# Revit family: Projector-DLP-Panasonic-1_Chip-Full_Brightness-Longer_Lasting_Laser_Performance-PT-FRZ60_SeriesX
name_source: partatom
category: Communication Devices
units: mm (PartAtom-declared; Revit-internal decimal feet)

## family parameters
Cut with Voids When Loaded = Yes
Host = Face
Maintain Annotation Orientation = No
OmniClass Number = 23.85.10.17.11.21
OmniClass Title = Data/Multi/Media Projectors
Part Type = Normal
Room Calculation Point = No
Round Connector Dimension = Use Diameter
Shared = No

## types (2) — shared parameters
352_mm = High_Ceiling_Height : 352_mm
392_mm = High_Ceiling_Height : 392_mm
432_mm = High_Ceiling_Height : 432_mm
A_Supplied_Max = 2.5118
A_Supplied_Min = 1.2598
Body Depth = 460 mm  [stored 1.50919 ft]
Ceiling Distance = 100 mm  [stored 0.328084 ft]
Chip Diagonal = 17 mm
Chip Quantity = 1
Clearance Value = 500 mm  [stored 1.64042 ft]
Const Length Projector Pan Handle = 2000 mm  [stored 6.56168 ft]
Const Length Projector Panning Base = 1000 mm  [stored 3.28084 ft]
Contrast Ratio = 20000
Date Last Modified = 2020/10/14
Depth = 492 mm
Equipment Abbreviation = LVP
Family Version = 1.0.0
HDMI In = HDMI 19-pin x 2 Compatible with HDCP 2.3, Deep Color, 4K/60p signal input*6, CEC supported
Height = 168 mm  [stored 0.551181 ft]
LAN = RJ‑45 x 1 for network connection, PJLink (class 2) compatible, 10Base‑T/100Base‑TX, Art-Net compatible
Lamp Life Economy = 24000
Lamp Life Full = 20000
Lamp Type = Laser diodes
Lens Type = Integrated
Manufacturer = Panasonic
Market = Commercial
Max Air Exhaust Volume = 285.00 CFM
Model Disclaimer = Contact Panasonic for more information
Motorized Zoom = No
Must be Level = No
Panasonic Logo Material = Paint - Panasonic Logo
Power Standby Eco = 1 W
Power Standby Normal = 10 W
Product Documentation Link = https://bizpartner.panasonic.net
Product Material = Plastic - Panasonic White
Product Page URL = https://panasonic.net
Provide Feedback = https://www.surveymonkey.com
Resolution Horizontal = 1920
Resolution Vertical = 1200
Technology = DLP™ chip x 1, DLP™ projection system
Temperature Max = 113 °F
Temperature Min = 32 °F
URL = http://panasonic.net
Width = 498 mm  [stored 1.63386 ft]
zero-valued in all types: Default Elevation

## per-type parameters (varying)
| type | Brightness Economy | Brightness Full | Description | Heat Load Active | Lamp Quantity | Noise in High Mode | Noise in Low Mode | P Type | Part Description | Power Active | Total Rated Watts | Weight |
| PT-FRZ60 | 4800 lm | 6000 lm | 6,000 Lumens, 16:10 Aspect Ratio, WUXGA, Projector, PT-FRZ60 | 1843.00 Btu/h | 4 | 35 | 30 | 60 | 6,000 Lumens, 16:10 Aspect Ratio, WUXGA, Projector, PT-FRZ60 | 540 W | 540 W | 35.50 lb |
| PT-FRZ50 | 4100 lm | 5200 lm | 5,200 Lumens, 16:10 Aspect Ratio, WUXGA, Projector, PT-FRZ50 | 1587.00 Btu/h | 2 | 32 | 27 | 50 | 5,200 Lumens, 16:10 Aspect Ratio, WUXGA, Projector, PT-FRZ50 | 465 W | 465 W | 35.30 lb |

note: column(s) folded — value = type name in every type: Model, Part Number

note: [stored X ft] marks values corroborated as IEEE doubles in the binary element streams (Revit-internal decimal feet)

## geometry (parser evidence)
native form markers: Blend x2, Sweep x9
no freeform markers — native parametric forms only
